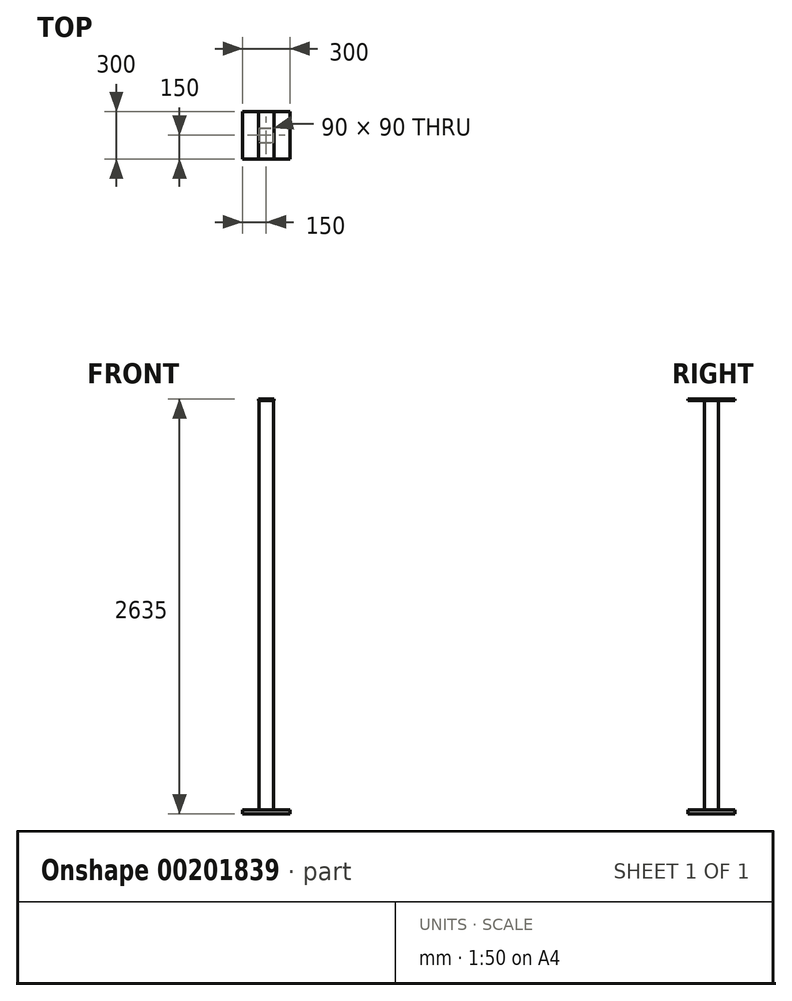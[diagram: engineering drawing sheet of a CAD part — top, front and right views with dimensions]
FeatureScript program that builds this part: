
annotation { "Feature Type Name" : "Feature", "Feature Type Description" : "" }
export const myFeature = defineFeature(function(context is Context, id is Id, definition is map)
    precondition{}
    {
        {
            var Q0;
            Q0=qCreatedBy(makeId("Top.planeOp"),FACE);
            var sketch = newSketch(context, id + "F0", { "sketchPlane" : qUnion([Q0])});
            skLineSegment(sketch, "E0.bottom", {"start": v(0, 0) * mm, "end": v(300, 0) * mm});
            skLineSegment(sketch, "E0.top", {"start": v(0, 300) * mm, "end": v(300, 300) * mm});
            skLineSegment(sketch, "E0.left", {"start": v(0, 0) * mm, "end": v(0, 300) * mm});
            skLineSegment(sketch, "E0.right", {"start": v(300, 0) * mm, "end": v(300, 300) * mm});
            skLineSegment(sketch, "E1", {"start": v(150, 300) * mm, "end": v(150, 0) * mm, "construction": true});
            skLineSegment(sketch, "E2", {"start": v(300, 150) * mm, "end": v(0, 150) * mm, "construction": true});
            skLineSegment(sketch, "E3.bottom", {"start": v(105, 195) * mm, "end": v(195, 195) * mm});
            skLineSegment(sketch, "E3.top", {"start": v(105, 105) * mm, "end": v(195, 105) * mm});
            skLineSegment(sketch, "E3.left", {"start": v(105, 195) * mm, "end": v(105, 105) * mm});
            skLineSegment(sketch, "E3.right", {"start": v(195, 195) * mm, "end": v(195, 105) * mm});
            skPoint(sketch, "E3.middle", {"position": v(150, 150) * mm});
            skSolve(sketch);
        }
        {
            var Q0;
            Q0=makeQuery(id+"F0.imprint","IMPRINT",FACE,{"disambiguationData":[TD([[makeQuery(id+"F0.imprint","IMPRINT",EDGE,{"derivedFrom":sQuery(id+"F0.wireOp",EDGE,"E0.bottom")}),1.0]])]});
            var Q1;
            Q1=makeQuery(id+"F0.imprint","IMPRINT",FACE,{"disambiguationData":[TD([[makeQuery(id+"F0.imprint","IMPRINT",EDGE,{"derivedFrom":sQuery(id+"F0.wireOp",EDGE,"E3.bottom")}),-1.0]])]});
            extrude(context, id + "F1", {"entities" : qUnion([Q0, Q1]), "oppositeDirection" : true, "depth" : 25 * mm});
        }
        {
            var Q0;
            Q0=makeQuery(id+"F0.imprint","IMPRINT",FACE,{"disambiguationData":[TD([[makeQuery(id+"F0.imprint","IMPRINT",EDGE,{"derivedFrom":sQuery(id+"F0.wireOp",EDGE,"E3.bottom")}),-1.0]])]});
            extrude(context, id + "F2", {"entities" : qUnion([Q0]), "operationType" : NewBodyOperationType.ADD, "depth" : 2600 * mm});
        }
        {
            var Q0;
            Q0=makeQuery(id+"F2.opExtrude","CAP_FACE",FACE,{"disambiguationData":[OSD([sQuery(id+"F0.wireOp",EDGE,"E3.bottom"),sQuery(id+"F0.wireOp",EDGE,"E3.top"),sQuery(id+"F0.wireOp",EDGE,"E3.left"),sQuery(id+"F0.wireOp",EDGE,"E3.right")])],"isStart":false});
            var sketch = newSketch(context, id + "F3", { "sketchPlane" : qUnion([Q0])});
            skPoint(sketch, "E4.0", {"position": v(0, 300) * mm});
            skPoint(sketch, "E5.0", {"position": v(300, 300) * mm});
            skPoint(sketch, "E6.0", {"position": v(300, 0) * mm});
            skPoint(sketch, "E7.0", {"position": v(0, 0) * mm});
            skLineSegment(sketch, "E8", {"start": v(100, 300) * mm, "end": v(200, 300) * mm});
            skLineSegment(sketch, "E9", {"start": v(200, 0) * mm, "end": v(100, 0) * mm});
            skLineSegment(sketch, "E10", {"start": v(100, 300) * mm, "end": v(100, 0) * mm});
            skLineSegment(sketch, "E11", {"start": v(200, 300) * mm, "end": v(200, 0) * mm});
            skSolve(sketch);
        }
        {
            var Q0;
            Q0 = qSketchRegion(id + "F3", true);
            extrude(context, id + "F4", {"entities" : qUnion([Q0]), "operationType" : NewBodyOperationType.ADD, "depth" : 10 * mm});
        }
    });
